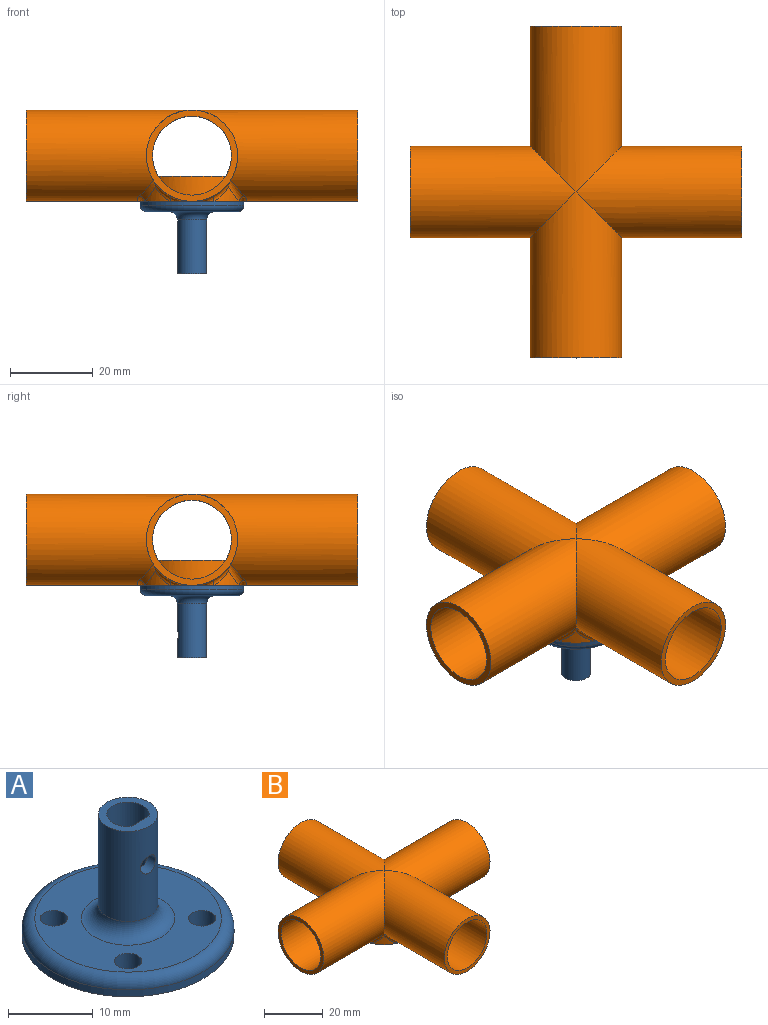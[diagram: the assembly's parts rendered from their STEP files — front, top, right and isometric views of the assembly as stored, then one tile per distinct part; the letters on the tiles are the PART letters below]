
ASSEMBLY  parts=2 mates=1
PART A: 15 faces, bbox 27.1x27.1x17.5 mm
  f0: cylinder r=3.5mm len=13mm, axis (0,0,-1), area 280.9mm2, adj f5,f9,f14
  f1: cylinder r=12.5mm len=25mm, axis (0,0,-1), area 78.5mm2, adj f3,f4
  f2: plane 22x22mm, normal (0,0,1), area 252.9mm2, adj f4,f9,f10,f11,f12,f13
  f3: plane 25x25mm, normal (0,0,-1), area 458.7mm2, adj f1,f10,f11,f12,f13
  f4: torus R=11mm, axis (0,0,1), area 177mm2, adj f1,f2
  f5: plane 7x7mm, normal (0,0,1), area 19.9mm2, adj f0,f6,f7
  f6: cylinder r=2.5mm len=15mm, axis (0,0,1), area 187.4mm2, adj f5,f7,f8
  f7: plane 15x3mm, normal (0,1,0), area 40.1mm2, adj f5,f6,f8,f14
  f8: plane 5x4.5mm, normal (0,0,1), area 18.6mm2, adj f6,f7
  f9: torus R=5.5mm, axis (0,0,1), area 83.4mm2, adj f0,f2
  f10: cylinder r=1.6mm len=3.2mm, axis (0,0,-1), area 25.1mm2, adj f2,f3
  f11: cylinder r=1.6mm len=3.2mm, axis (0,0,-1), area 25.1mm2, adj f2,f3
  f12: cylinder r=1.6mm len=3.2mm, axis (0,0,-1), area 25.1mm2, adj f2,f3
  f13: cylinder r=1.6mm len=3.2mm, axis (0,0,-1), area 25.1mm2, adj f2,f3
  f14: cylinder r=1.25mm len=2.5mm, axis (0,1,0), area 10.9mm2, adj f0,f7
PART B: 42 faces, bbox 80.2x80.2x22.8 mm
  f0: cylinder r=11mm len=40mm, axis (0,1,0), area 2133mm2, adj f5,f12,f13,f24,f25,f30,f31
  f1: cylinder r=11mm len=40mm, axis (0,1,0), area 2133mm2, adj f6,f12,f13,f28,f29,f36,f37
  f2: cylinder r=9.5mm len=40mm, axis (1,0,0), area 1899.3mm2, adj f4,f7,f17,f19,f21
  f3: cylinder r=9.5mm len=40mm, axis (1,0,0), area 1899.3mm2, adj f4,f7,f18,f20,f21
  f4: cylinder r=9.5mm len=40mm, axis (0,-1,0), area 1899.3mm2, adj f2,f3,f5,f9,f21
  f5: plane 22x22mm, normal (0,-1,0), area 96.6mm2, adj f0,f4
  f6: plane 22x22mm, normal (0,1,0), area 96.6mm2, adj f1,f7
  f7: cylinder r=9.5mm len=40mm, axis (0,-1,0), area 1899.3mm2, adj f2,f3,f6,f16,f21
  f8: plane 25.23x25.23mm, normal (0,0,-1), area 454.6mm2, adj f10,f11,f14,f15,f22,f24,f26,f29
  f9: cylinder r=12.5mm len=16.16mm, axis (0,0,-1), area 39.5mm2, adj f4,f21
  f10: cylinder r=12.5mm len=6.02mm, axis (0,0,-1), area 14.6mm2, adj f8,f23,f25
  f11: cylinder r=12.5mm len=6.02mm, axis (0,0,-1), area 14.6mm2, adj f8,f31,f33
  f12: cylinder r=11mm len=40mm, axis (-1,0,0), area 2133mm2, adj f0,f1,f17,f22,f23,f26,f27
  f13: cylinder r=11mm len=40mm, axis (-1,0,0), area 2133mm2, adj f0,f1,f18,f32,f33,f34,f35
  f14: cylinder r=12.5mm len=6.02mm, axis (0,0,-1), area 14.6mm2, adj f8,f35,f37
  f15: cylinder r=12.5mm len=6.02mm, axis (0,0,-1), area 14.6mm2, adj f8,f27,f28
  f16: cylinder r=12.5mm len=16.16mm, axis (0,0,-1), area 39.5mm2, adj f7,f21
  f17: plane 22x22mm, normal (1,0,0), area 96.6mm2, adj f2,f12
  f18: plane 22x22mm, normal (-1,0,0), area 96.6mm2, adj f3,f13
  f19: cylinder r=12.5mm len=16.16mm, axis (0,0,-1), area 39.5mm2, adj f2,f21
  f20: cylinder r=12.5mm len=16.16mm, axis (0,0,-1), area 39.5mm2, adj f3,f21
  f21: plane 25x25mm, normal (0,0,1), area 450mm2, adj f2,f3,f4,f7,f9,f16,f19,f20
  f22: bspline ~5.52x1.95mm, area 3.5mm2, adj f8,f12,f23
  f23: bspline ~6.05x5.83mm, area 10.3mm2, adj f10,f12,f22,f25
  f24: bspline ~5.52x1.95mm, area 3.5mm2, adj f0,f8,f25
  f25: bspline ~6.05x5.83mm, area 10.3mm2, adj f0,f10,f23,f24
  f26: bspline ~5.52x1.95mm, area 3.5mm2, adj f8,f12,f27
  f27: bspline ~6.05x5.83mm, area 10.3mm2, adj f12,f15,f26,f28
  f28: bspline ~6.05x5.83mm, area 10.3mm2, adj f1,f15,f27,f29
  f29: bspline ~5.52x1.95mm, area 3.5mm2, adj f1,f8,f28
  f30: bspline ~5.52x1.95mm, area 3.5mm2, adj f0,f8,f31
  f31: bspline ~6.05x5.83mm, area 10.3mm2, adj f0,f11,f30,f33
  f32: bspline ~5.52x1.95mm, area 3.5mm2, adj f8,f13,f33
  f33: bspline ~6.05x5.83mm, area 10.3mm2, adj f11,f13,f31,f32
  f34: bspline ~5.52x1.95mm, area 3.5mm2, adj f8,f13,f35
  f35: bspline ~6.05x5.83mm, area 10.3mm2, adj f13,f14,f34,f37
  f36: bspline ~5.52x1.95mm, area 3.5mm2, adj f1,f8,f37
  f37: bspline ~6.05x5.83mm, area 10.3mm2, adj f1,f14,f35,f36
  f38: cylinder r=1.7mm len=6mm, axis (0,0,-1), area 64.1mm2, adj f8,f21
  f39: cylinder r=1.7mm len=6mm, axis (0,0,-1), area 64.1mm2, adj f8,f21
  f40: cylinder r=1.7mm len=6mm, axis (0,0,-1), area 64.1mm2, adj f8,f21
  f41: cylinder r=1.7mm len=6mm, axis (0,0,-1), area 64.1mm2, adj f8,f21
PLACE A rot(axis=(1,0,0),180deg) t=(0,0,-11)mm
PLACE B at identity
MATE fastened A.f1 <-> B.f9  axis (0,0,-1) through (0,0,-11)mm
